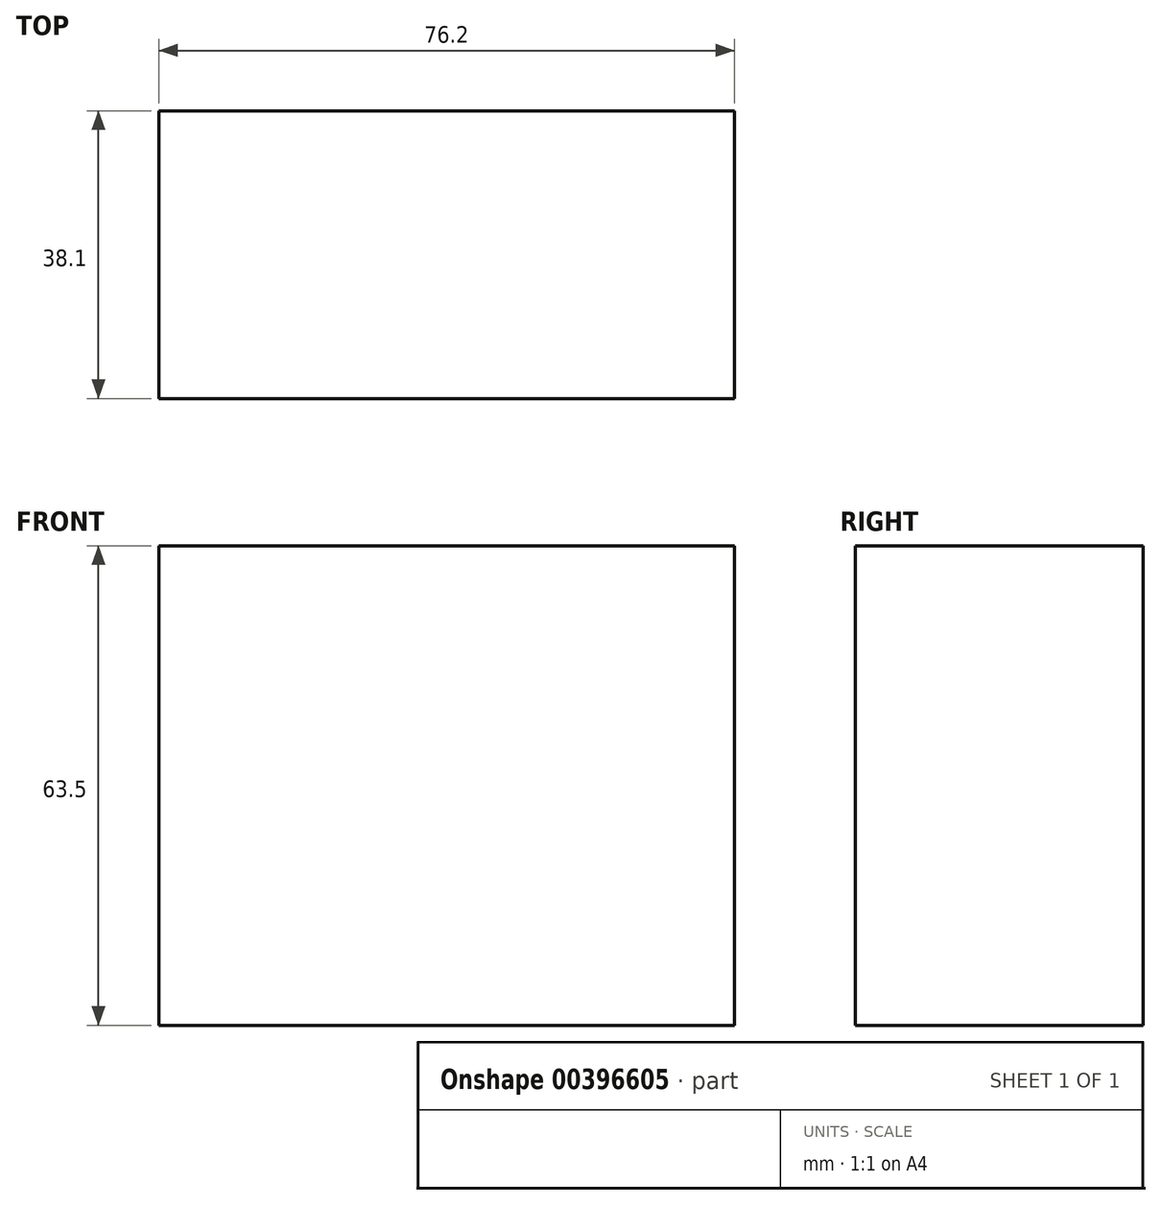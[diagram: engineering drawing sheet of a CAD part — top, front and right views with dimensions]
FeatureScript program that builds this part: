
annotation { "Feature Type Name" : "Feature", "Feature Type Description" : "" }
export const myFeature = defineFeature(function(context is Context, id is Id, definition is map)
    precondition{}
    {
        {
            var Q0;
            Q0=qCreatedBy(makeId("Front.planeOp"),FACE);
            var sketch = newSketch(context, id + "F0", { "sketchPlane" : qUnion([Q0])});
            skLineSegment(sketch, "E0.bottom", {"start": v(-38.1, 31.75) * mm, "end": v(38.1, 31.75) * mm});
            skLineSegment(sketch, "E0.top", {"start": v(-38.1, -31.75) * mm, "end": v(38.1, -31.75) * mm});
            skLineSegment(sketch, "E0.left", {"start": v(-38.1, 31.75) * mm, "end": v(-38.1, -31.75) * mm});
            skLineSegment(sketch, "E0.right", {"start": v(38.1, 31.75) * mm, "end": v(38.1, -31.75) * mm});
            skPoint(sketch, "E0.middle", {"position": v(0, 0) * mm});
            skLineSegment(sketch, "E1.bottom", {"start": v(-50.8, 38.1) * mm, "end": v(50.8, 38.1) * mm});
            skLineSegment(sketch, "E1.top", {"start": v(-50.8, -38.1) * mm, "end": v(50.8, -38.1) * mm});
            skLineSegment(sketch, "E1.left", {"start": v(-50.8, 38.1) * mm, "end": v(-50.8, -38.1) * mm});
            skLineSegment(sketch, "E1.right", {"start": v(50.8, 38.1) * mm, "end": v(50.8, -38.1) * mm});
            skSolve(sketch);
        }
        {
            var Q0;
            Q0=makeQuery(id+"F0.imprint","IMPRINT",FACE,{"disambiguationData":[TD([[makeQuery(id+"F0.imprint","IMPRINT",EDGE,{"derivedFrom":sQuery(id+"F0.wireOp",EDGE,"E0.bottom")}),-1.0]])]});
            extrude(context, id + "F1", {"entities" : qUnion([Q0]), "depth" : 38.1 * mm});
        }
        {
            var Q0;
            Q0=sQuery(id+"F0.wireOp",EDGE,"E1.bottom");
            var Q1;
            Q1=sQuery(id+"F0.wireOp",EDGE,"E1.right");
            var Q2;
            Q2=sQuery(id+"F0.wireOp",EDGE,"E1.top");
            var Q3;
            Q3=sQuery(id+"F0.wireOp",EDGE,"E1.left");
            extrude(context, id + "F2", {"bodyType" : ToolBodyType.SURFACE, "surfaceEntities" : qUnion([Q0, Q1, Q2, Q3]), "depth" : 50.8 * mm});
        }
    });
